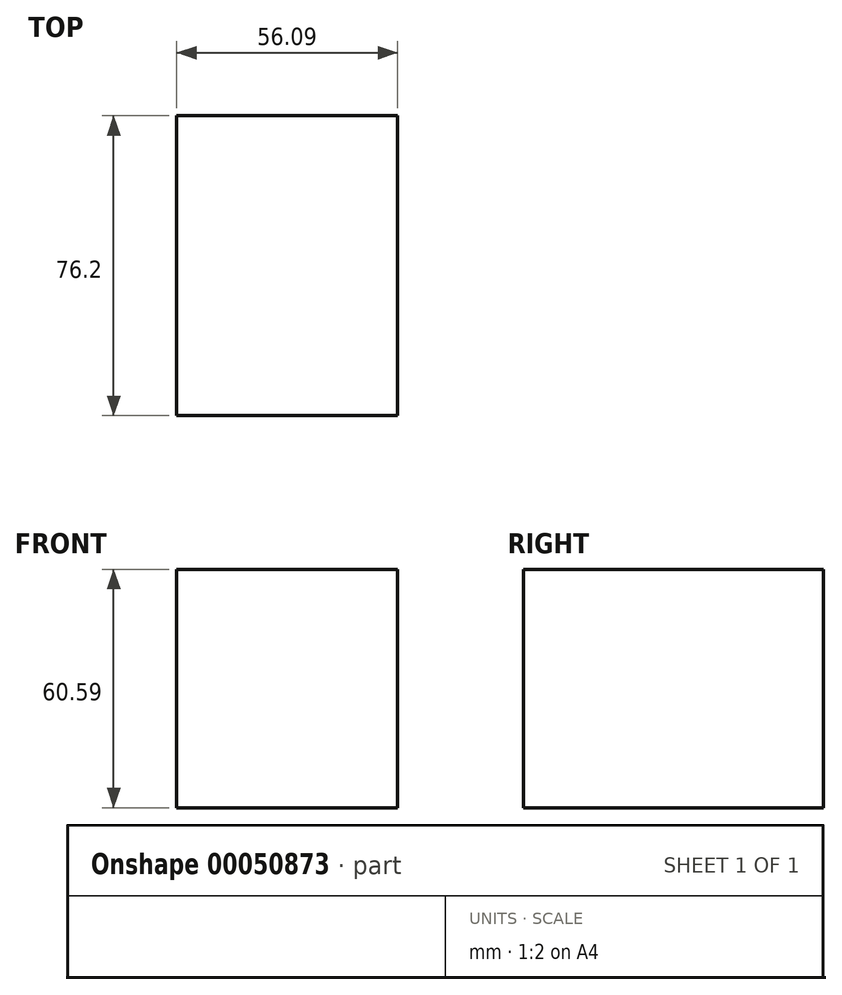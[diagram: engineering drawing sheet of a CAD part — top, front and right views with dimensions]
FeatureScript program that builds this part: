
annotation { "Feature Type Name" : "Feature", "Feature Type Description" : "" }
export const myFeature = defineFeature(function(context is Context, id is Id, definition is map)
    precondition{}
    {
        {
            var Q0;
            Q0=qCreatedBy(makeId("Front.planeOp"),FACE);
            var sketch = newSketch(context, id + "F0", { "sketchPlane" : qUnion([Q0])});
            skLineSegment(sketch, "E0.bottom", {"start": v(-66.64, 60.59) * mm, "end": v(-10.55, 60.59) * mm});
            skLineSegment(sketch, "E0.top", {"start": v(-66.64, 0) * mm, "end": v(-10.55, 0) * mm});
            skLineSegment(sketch, "E0.left", {"start": v(-66.64, 60.59) * mm, "end": v(-66.64, 0) * mm});
            skLineSegment(sketch, "E0.right", {"start": v(-10.55, 60.59) * mm, "end": v(-10.55, 0) * mm});
            skSolve(sketch);
        }
        {
            var Q0;
            Q0=makeQuery(id+"F0.imprint","IMPRINT",FACE,{"disambiguationData":[TD([[makeQuery(id+"F0.imprint","IMPRINT",EDGE,{"derivedFrom":sQuery(id+"F0.wireOp",EDGE,"E0.bottom")}),-1.0]])]});
            extrude(context, id + "F1", {"entities" : qUnion([Q0]), "depth" : 76.2 * mm});
        }
        {
            var Q0;
            Q0=makeQuery(id+"F1.opExtrude","CAP_FACE",FACE,{"disambiguationData":[OSD([sQuery(id+"F0.wireOp",EDGE,"E0.bottom"),sQuery(id+"F0.wireOp",EDGE,"E0.top"),sQuery(id+"F0.wireOp",EDGE,"E0.left"),sQuery(id+"F0.wireOp",EDGE,"E0.right")])],"isStart":false});
            var sketch = newSketch(context, id + "F2", { "sketchPlane" : qUnion([Q0])});
            skCircle(sketch, "E1", {"center": v(-54.41, 48.65) * mm, "radius": 6.17 * mm});
            skCircle(sketch, "E2", {"center": v(-24.66, 47.58) * mm, "radius": 7.08 * mm});
            skCircle(sketch, "E3", {"center": v(-49.86, 17.82) * mm, "radius": 7.77 * mm});
            skCircle(sketch, "E4", {"center": v(-24.12, 19.43) * mm, "radius": 7.55 * mm});
            skSolve(sketch);
        }
        {
            var Q0;
            Q0=makeQuery(id+"F2.imprint","IMPRINT",FACE,{"disambiguationData":[TD([[makeQuery(id+"F2.imprint","IMPRINT",EDGE,{"derivedFrom":sQuery(id+"F2.wireOp",EDGE,"E2")}),1.0]])]});
            extrude(context, id + "F3", {"entities" : qUnion([Q0]), "operationType" : NewBodyOperationType.ADD, "depth" : 12.7 * mm});
        }
        {
            var Q0;
            Q0=makeQuery(id+"F3.opExtrude","CAP_FACE",FACE,{"disambiguationData":[OSD([sQuery(id+"F2.wireOp",EDGE,"E2")])],"isStart":false});
            var Q1;
            Q1=makeQuery(id+"F1.opExtrude","CAP_FACE",FACE,{"disambiguationData":[OSD([sQuery(id+"F0.wireOp",EDGE,"E0.bottom"),sQuery(id+"F0.wireOp",EDGE,"E0.top"),sQuery(id+"F0.wireOp",EDGE,"E0.left"),sQuery(id+"F0.wireOp",EDGE,"E0.right")])],"isStart":true});
            extrude(context, id + "F4", {"entities" : qUnion([Q0, Q1]), "operationType" : NewBodyOperationType.REMOVE, "oppositeDirection" : true, "depth" : 12.7 * mm});
        }
    });
